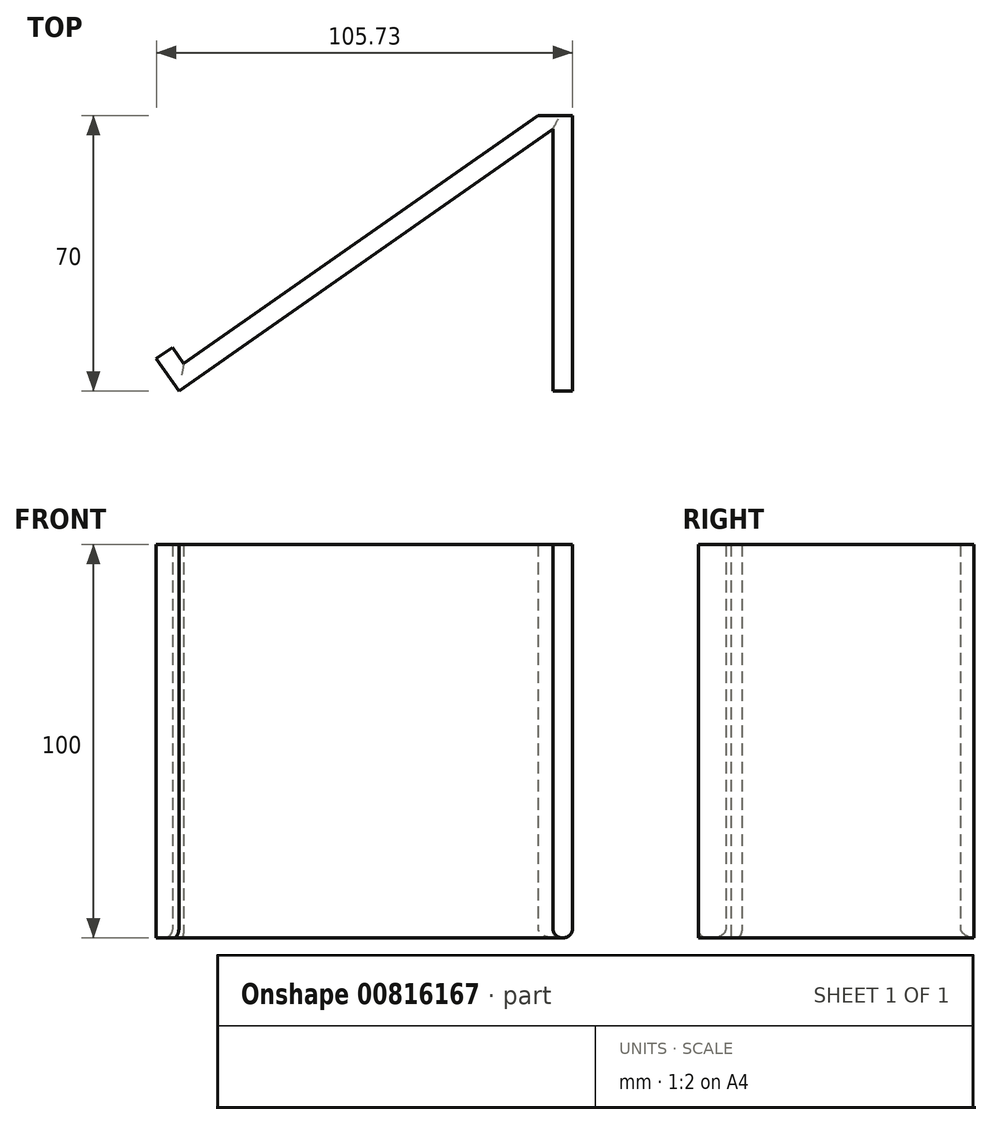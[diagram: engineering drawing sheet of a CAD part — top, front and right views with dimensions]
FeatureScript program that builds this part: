
annotation { "Feature Type Name" : "Feature", "Feature Type Description" : "" }
export const myFeature = defineFeature(function(context is Context, id is Id, definition is map)
    precondition{}
    {
        {
            var Q0;
            Q0=qCreatedBy(makeId("Top.planeOp"),FACE);
            var sketch = newSketch(context, id + "F0", { "sketchPlane" : qUnion([Q0])});
            skLineSegment(sketch, "E0.bottom", {"start": v(-50, 35) * mm, "end": v(50, 35) * mm});
            skLineSegment(sketch, "E0.top", {"start": v(-50, -35) * mm, "end": v(50, -35) * mm});
            skLineSegment(sketch, "E0.left", {"start": v(-50, 35) * mm, "end": v(-50, -26.28) * mm});
            skLineSegment(sketch, "E0.right", {"start": v(50, 35) * mm, "end": v(50, -35) * mm});
            skPoint(sketch, "E0.middle", {"position": v(0, 0) * mm});
            skLineSegment(sketch, "E1", {"start": v(-50, -35) * mm, "end": v(45, 31.5) * mm});
            skLineSegment(sketch, "E2", {"start": v(-50, -35) * mm, "end": v(-52.87, -30.9) * mm});
            skLineSegment(sketch, "E3", {"start": v(-48.77, -28.04) * mm, "end": v(41.28, 35) * mm});
            skLineSegment(sketch, "E4", {"start": v(-52.87, -30.9) * mm, "end": v(-55.73, -26.8) * mm});
            skLineSegment(sketch, "E5", {"start": v(-55.73, -26.8) * mm, "end": v(-51.64, -23.94) * mm});
            skLineSegment(sketch, "E6", {"start": v(-51.64, -23.94) * mm, "end": v(-48.77, -28.04) * mm});
            skLineSegment(sketch, "E7", {"start": v(50, -35) * mm, "end": v(45, -35) * mm});
            skLineSegment(sketch, "E8", {"start": v(45, -35) * mm, "end": v(45, 31.5) * mm});
            skPoint(sketch, "E9.orphan", {"position": v(45, 35) * mm});
            skSolve(sketch);
        }
        {
            var Q0;
            {var subQ4=sQuery(id+"F0.wireOp",EDGE,"E0.right");Q0=makeQuery(id+"F0.imprint","IMPRINT",FACE,{"disambiguationData":[TD([[makeQuery(id+"F0.imprint","IMPRINT",EDGE,{"derivedFrom":subQ4}),-1.0]])]});}
            extrude(context, id + "F1", {"entities" : qUnion([Q0]), "depth" : 50 * mm, "offsetDistance" : 25 * mm, "hasSecondDirection" : true, "secondDirectionOppositeDirection" : true, "secondDirectionDepth" : 50 * mm});
        }
        {
            var Q0;
            Q0=makeQuery(id+"F1.opExtrude","CAP_EDGE",EDGE,{"disambiguationData":[OSD([sQuery(id+"F0.wireOp",EDGE,"E0.right")])],"isStart":true});
            var Q1;
            Q1=makeQuery(id+"F1.opExtrude","CAP_EDGE",EDGE,{"disambiguationData":[OSD([sQuery(id+"F0.wireOp",EDGE,"E8")])],"isStart":true});
            var Q2;
            Q2=makeQuery(id+"F1.opExtrude","CAP_EDGE",EDGE,{"disambiguationData":[OSD([sQuery(id+"F0.wireOp",EDGE,"E1")])],"isStart":true});
            var Q3;
            Q3=makeQuery(id+"F1.opExtrude","CAP_EDGE",EDGE,{"disambiguationData":[OSD([sQuery(id+"F0.wireOp",EDGE,"E3")])],"isStart":true});
            var Q4;
            Q4=makeQuery(id+"F1.opExtrude","CAP_EDGE",EDGE,{"disambiguationData":[OSD([sQuery(id+"F0.wireOp",EDGE,"E6")])],"isStart":true});
            fillet(context, id + "F2", {"entities" : qUnion([Q0, Q1, Q2, Q3, Q4]), "radius" : 2.5 * mm, "tangentPropagation" : true, "allowEdgeOverflow" : false});
        }
    });
